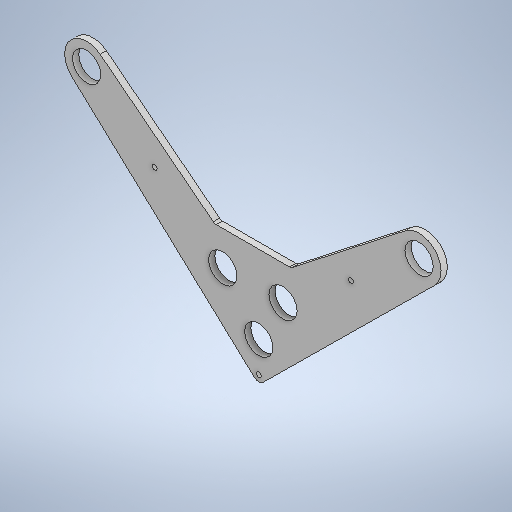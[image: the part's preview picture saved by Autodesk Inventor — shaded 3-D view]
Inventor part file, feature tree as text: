
AUTODESK INVENTOR PART (.ipt)
format: ipt  version: 2025.1 (Build 291241020, 241B)  size: 302,080 bytes
history: native  units: in
note: dims shown in document units (in); Inventor stores cm internally (conversion verified against a paired STEP export)
features: sketch x1, extrude x1
ambient origin geometry x8: Origin, YZ Plane, XZ Plane, XY Plane, X Axis, Y Axis, Z Axis, Center Point
bodies: Solid1 (feature_tree)
feature tree (2):
  sketch  "Sketch1"  dims[d0=4.0in d1=4.0in d2=0.196in d3=0.5in d4=3.4395in d5=0.5in d6=0.063in d7=0.196in d8=0.5in d9=0.196in d10=3.4395in d11=0.063in d12=0.188in d13=1.75in d14=1.75in d15=1.125in d16=0.7146in d17=6.879in d18=1.654in d19=1.504in d20=1.125in d21=0.063in d22=0.1in d23=2.4in d24=0.1in d25=1.6in d27=0.0in d28=0.25in]
  extrude  "Extrusion1"  [1 undecoded]
note: 1 required parameter value undecoded (feature->parameter linkage not recoverable at this tier; creation-order binding heuristic only, values carry confidence <= 0.55)
